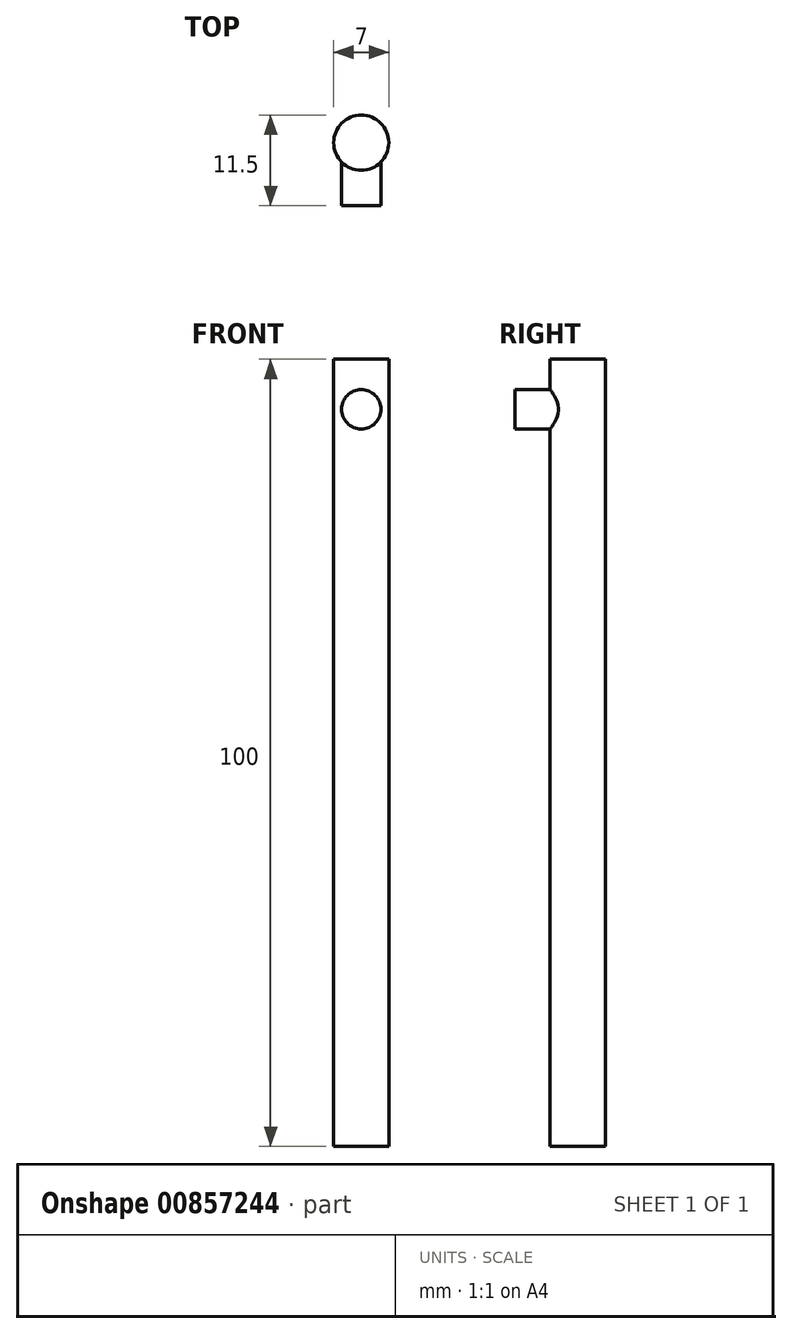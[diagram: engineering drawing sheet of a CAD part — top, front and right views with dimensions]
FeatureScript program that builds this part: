
annotation { "Feature Type Name" : "Feature", "Feature Type Description" : "" }
export const myFeature = defineFeature(function(context is Context, id is Id, definition is map)
    precondition{}
    {
        {
            var Q0;
            Q0=qCreatedBy(makeId("Top.planeOp"),FACE);
            var sketch = newSketch(context, id + "F0", { "sketchPlane" : qUnion([Q0])});
            skCircle(sketch, "E0", {"center": v(0, 0) * mm, "radius": 3.5 * mm});
            skSolve(sketch);
        }
        {
            var Q0;
            Q0 = qSketchRegion(id + "F0", true);
            extrude(context, id + "F1", {"entities" : qUnion([Q0]), "depth" : 100 * mm, "offsetDistance" : 25 * mm});
        }
        {
            var Q0;
            Q0=qCreatedBy(makeId("Front.planeOp"),FACE);
            var sketch = newSketch(context, id + "F2", { "sketchPlane" : qUnion([Q0])});
            skCircle(sketch, "E1", {"center": v(0, 93.63) * mm, "radius": 2.5 * mm});
            skSolve(sketch);
        }
        {
            var Q0;
            Q0 = qSketchRegion(id + "F2", true);
            extrude(context, id + "F3", {"entities" : qUnion([Q0]), "operationType" : NewBodyOperationType.ADD, "depth" : 8 * mm, "offsetDistance" : 25 * mm});
        }
    });
